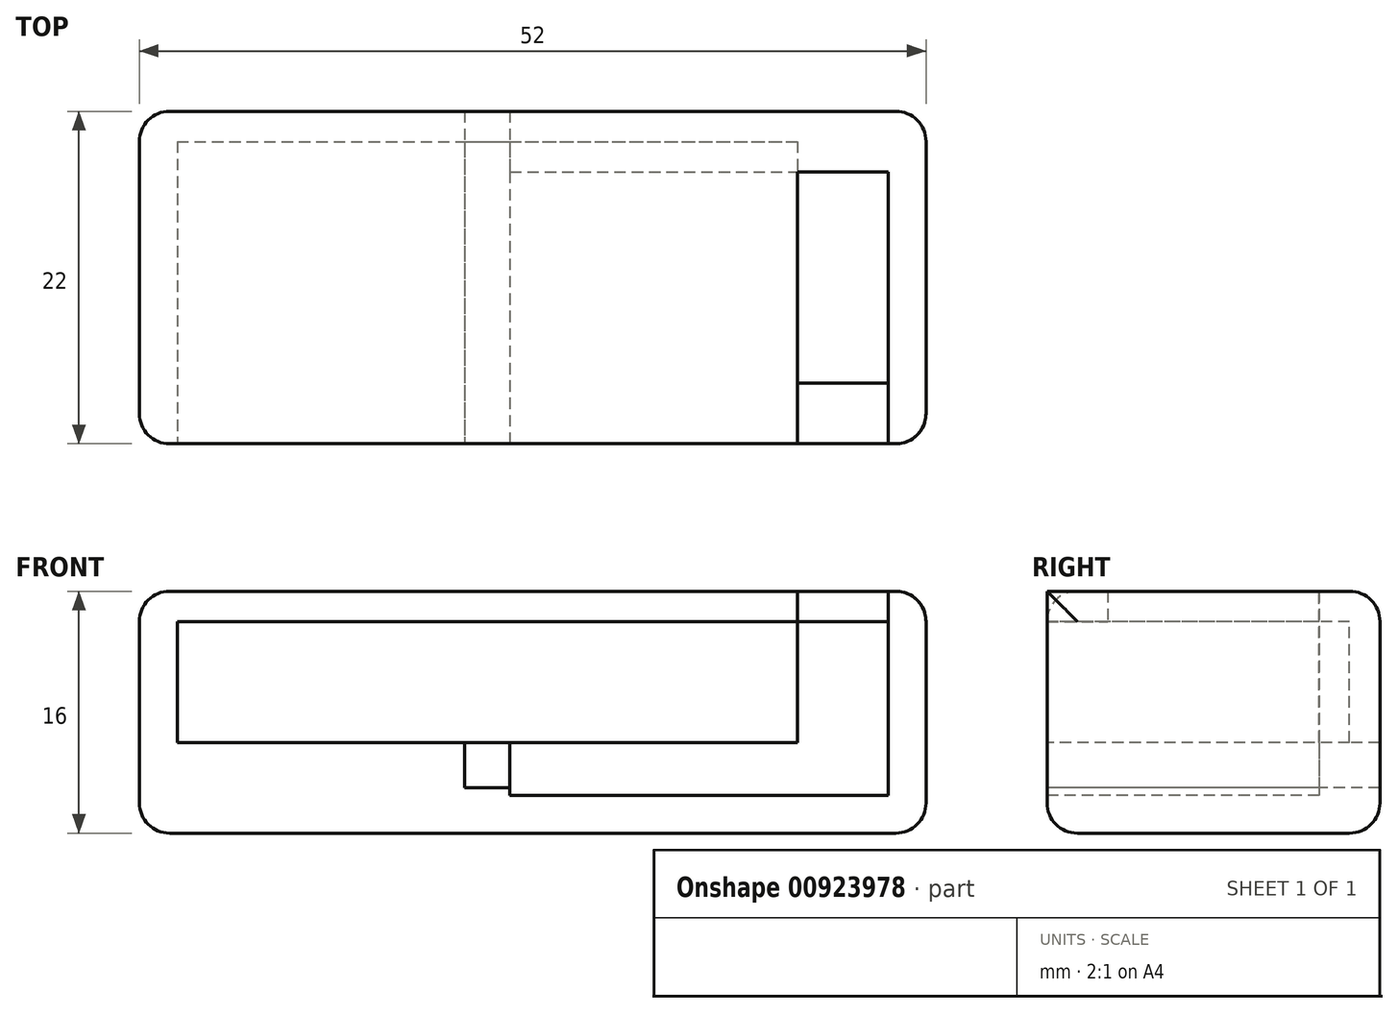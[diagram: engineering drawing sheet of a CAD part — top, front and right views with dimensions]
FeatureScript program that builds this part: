
annotation { "Feature Type Name" : "Feature", "Feature Type Description" : "" }
export const myFeature = defineFeature(function(context is Context, id is Id, definition is map)
    precondition{}
    {
        {
            var Q0;
            Q0=qCreatedBy(makeId("Top.planeOp"),FACE);
            var sketch = newSketch(context, id + "F0", { "sketchPlane" : qUnion([Q0])});
            skLineSegment(sketch, "E0.bottom", {"start": v(26, -11) * mm, "end": v(-26, -11) * mm});
            skLineSegment(sketch, "E0.top", {"start": v(26, 11) * mm, "end": v(-26, 11) * mm});
            skLineSegment(sketch, "E0.left", {"start": v(26, -11) * mm, "end": v(26, 11) * mm});
            skLineSegment(sketch, "E0.right", {"start": v(-26, -11) * mm, "end": v(-26, 11) * mm});
            skPoint(sketch, "E0.middle", {"position": v(0, 0) * mm});
            skSolve(sketch);
        }
        {
            var Q0;
            Q0 = qSketchRegion(id + "F0", true);
            extrude(context, id + "F1", {"entities" : qUnion([Q0]), "depth" : 16 * mm, "offsetDistance" : 25 * mm});
        }
        {
            var Q0;
            Q0=makeQuery(id+"F1.opExtrude","SWEPT_FACE",FACE,{"disambiguationData":[OSD([sQuery(id+"F0.wireOp",EDGE,"E0.bottom")])]});
            var sketch = newSketch(context, id + "F2", { "sketchPlane" : qUnion([Q0])});
            skLineSegment(sketch, "E1.bottom", {"start": v(-23.5, 6) * mm, "end": v(17.5, 6) * mm});
            skLineSegment(sketch, "E1.top", {"start": v(-23.5, 14) * mm, "end": v(17.5, 14) * mm});
            skLineSegment(sketch, "E1.left", {"start": v(-23.5, 6) * mm, "end": v(-23.5, 14) * mm});
            skLineSegment(sketch, "E1.right", {"start": v(17.5, 6) * mm, "end": v(17.5, 14) * mm});
            skSolve(sketch);
        }
        {
            var Q0;
            Q0 = qSketchRegion(id + "F2", true);
            extrude(context, id + "F3", {"entities" : qUnion([Q0]), "operationType" : NewBodyOperationType.REMOVE, "oppositeDirection" : true, "depth" : 20 * mm, "offsetDistance" : 25 * mm});
        }
        {
            var Q0;
            Q0=makeQuery(id+"F1.opExtrude","SWEPT_FACE",FACE,{"disambiguationData":[OSD([sQuery(id+"F0.wireOp",EDGE,"E0.bottom")])]});
            var sketch = newSketch(context, id + "F4", { "sketchPlane" : qUnion([Q0])});
            skLineSegment(sketch, "E2.bottom", {"start": v(-1.5, 6) * mm, "end": v(23.5, 6) * mm});
            skLineSegment(sketch, "E2.top", {"start": v(-1.5, 2.5) * mm, "end": v(23.5, 2.5) * mm});
            skLineSegment(sketch, "E2.left", {"start": v(-1.5, 6) * mm, "end": v(-1.5, 2.5) * mm});
            skLineSegment(sketch, "E2.right", {"start": v(23.5, 6) * mm, "end": v(23.5, 2.5) * mm});
            skLineSegment(sketch, "E3.bottom", {"start": v(17.5, 6) * mm, "end": v(23.5, 6) * mm});
            skLineSegment(sketch, "E3.top", {"start": v(17.5, 16) * mm, "end": v(23.5, 16) * mm});
            skLineSegment(sketch, "E3.left", {"start": v(17.5, 6) * mm, "end": v(17.5, 16) * mm});
            skLineSegment(sketch, "E3.right", {"start": v(23.5, 6) * mm, "end": v(23.5, 16) * mm});
            skSolve(sketch);
        }
        {
            var Q0;
            Q0 = qSketchRegion(id + "F4", true);
            extrude(context, id + "F5", {"entities" : qUnion([Q0]), "operationType" : NewBodyOperationType.REMOVE, "oppositeDirection" : true, "depth" : 18 * mm, "offsetDistance" : 25 * mm});
        }
        {
            var Q0;
            Q0=makeQuery(id+"F1.opExtrude","SWEPT_FACE",FACE,{"disambiguationData":[OSD([sQuery(id+"F0.wireOp",EDGE,"E0.bottom")])]});
            var sketch = newSketch(context, id + "F6", { "sketchPlane" : qUnion([Q0])});
            skLineSegment(sketch, "E4.bottom", {"start": v(-1.5, 6) * mm, "end": v(-4.5, 6) * mm});
            skLineSegment(sketch, "E4.top", {"start": v(-1.5, 3) * mm, "end": v(-4.5, 3) * mm});
            skLineSegment(sketch, "E4.left", {"start": v(-1.5, 6) * mm, "end": v(-1.5, 3) * mm});
            skLineSegment(sketch, "E4.right", {"start": v(-4.5, 6) * mm, "end": v(-4.5, 3) * mm});
            skSolve(sketch);
        }
        {
            var Q0;
            Q0 = qSketchRegion(id + "F6", true);
            extrude(context, id + "F7", {"entities" : qUnion([Q0]), "operationType" : NewBodyOperationType.REMOVE, "endBound" : BoundingType.UP_TO_NEXT, "oppositeDirection" : true, "depth" : 25 * mm, "offsetDistance" : 25 * mm});
        }
        {
            var Q0;
            Q0=makeQuery(id+"F5.boolean.opBoolean","COPY",FACE,{"derivedFrom":makeQuery(id+"F5.opExtrude","SWEPT_FACE",FACE,{"disambiguationData":[OSD([sQuery(id+"F4.wireOp",EDGE,"E2.right"),sQuery(id+"F4.wireOp",EDGE,"E3.right")])]})});
            var sketch = newSketch(context, id + "F8", { "sketchPlane" : qUnion([Q0])});
            skLineSegment(sketch, "E5.bottom", {"start": v(11, 16) * mm, "end": v(7, 16) * mm});
            skLineSegment(sketch, "E5.top", {"start": v(11, 14) * mm, "end": v(7, 14) * mm});
            skLineSegment(sketch, "E5.left", {"start": v(11, 16) * mm, "end": v(11, 14) * mm});
            skLineSegment(sketch, "E5.right", {"start": v(7, 16) * mm, "end": v(7, 14) * mm});
            skSolve(sketch);
        }
        {
            var Q0;
            Q0 = qSketchRegion(id + "F8", true);
            extrude(context, id + "F9", {"entities" : qUnion([Q0]), "depth" : 6 * mm, "offsetDistance" : 25 * mm});
        }
        {
            var Q0;
            Q0=makeQuery(id+"F1.opExtrude","CAP_EDGE",EDGE,{"disambiguationData":[OSD([sQuery(id+"F0.wireOp",EDGE,"E0.right")])],"isStart":true});
            var Q1;
            Q1=makeQuery(id+"F1.opExtrude","SWEPT_EDGE",EDGE,{"disambiguationData":[OSD([sQuery(id+"F0.wireOp",EDGE,"E0.bottom"),sQuery(id+"F0.wireOp",EDGE,"E0.right")])]});
            var Q2;
            {var subQ0=sQuery(id+"F0.wireOp",EDGE,"E0.bottom");var subQ1=sQuery(id+"F0.wireOp",EDGE,"E0.right");Q2=makeQuery(id+"F5.boolean.opBoolean","SPLIT",EDGE,{"disambiguationData":[TD([makeQuery(id+"F1.opExtrude","SWEPT_FACE",FACE,{"disambiguationData":[OSD([subQ1])]})])],"derivedFrom":makeQuery(id+"F1.opExtrude","CAP_EDGE",EDGE,{"disambiguationData":[OSD([subQ0])],"isStart":false})});}
            var Q3;
            Q3=makeQuery(id+"F1.opExtrude","CAP_EDGE",EDGE,{"disambiguationData":[OSD([sQuery(id+"F0.wireOp",EDGE,"E0.right")])],"isStart":false});
            var Q4;
            Q4=makeQuery(id+"F1.opExtrude","CAP_EDGE",EDGE,{"disambiguationData":[OSD([sQuery(id+"F0.wireOp",EDGE,"E0.bottom")])],"isStart":true});
            var Q5;
            Q5=makeQuery(id+"F1.opExtrude","SWEPT_EDGE",EDGE,{"disambiguationData":[OSD([sQuery(id+"F0.wireOp",EDGE,"E0.bottom"),sQuery(id+"F0.wireOp",EDGE,"E0.left")])]});
            var Q6;
            Q6=makeQuery(id+"F1.opExtrude","CAP_EDGE",EDGE,{"disambiguationData":[OSD([sQuery(id+"F0.wireOp",EDGE,"E0.left")])],"isStart":false});
            var Q7;
            Q7=makeQuery(id+"F1.opExtrude","SWEPT_EDGE",EDGE,{"disambiguationData":[OSD([sQuery(id+"F0.wireOp",EDGE,"E0.top"),sQuery(id+"F0.wireOp",EDGE,"E0.left")])]});
            var Q8;
            Q8=makeQuery(id+"F1.opExtrude","CAP_EDGE",EDGE,{"disambiguationData":[OSD([sQuery(id+"F0.wireOp",EDGE,"E0.left")])],"isStart":true});
            var Q9;
            Q9=makeQuery(id+"F1.opExtrude","CAP_EDGE",EDGE,{"disambiguationData":[OSD([sQuery(id+"F0.wireOp",EDGE,"E0.top")])],"isStart":false});
            var Q10;
            Q10=makeQuery(id+"F1.opExtrude","SWEPT_EDGE",EDGE,{"disambiguationData":[OSD([sQuery(id+"F0.wireOp",EDGE,"E0.top"),sQuery(id+"F0.wireOp",EDGE,"E0.right")])]});
            var Q11;
            Q11=makeQuery(id+"F1.opExtrude","CAP_EDGE",EDGE,{"disambiguationData":[OSD([sQuery(id+"F0.wireOp",EDGE,"E0.top")])],"isStart":true});
            var Q12;
            Q12=makeQuery(id+"F7.boolean.opBoolean","COPY",EDGE,{"derivedFrom":makeQuery(id+"F7.opExtrude","CAP_EDGE",EDGE,{"disambiguationData":[OSD([sQuery(id+"F6.wireOp",EDGE,"E4.bottom")])],"isStart":false})});
            var Q13;
            Q13=makeQuery(id+"F7.boolean.opBoolean","COPY",EDGE,{"derivedFrom":makeQuery(id+"F7.opExtrude","CAP_EDGE",EDGE,{"disambiguationData":[OSD([sQuery(id+"F6.wireOp",EDGE,"E4.right")])],"isStart":false})});
            var Q14;
            Q14=makeQuery(id+"F7.boolean.opBoolean","COPY",EDGE,{"derivedFrom":makeQuery(id+"F7.opExtrude","CAP_EDGE",EDGE,{"disambiguationData":[OSD([sQuery(id+"F6.wireOp",EDGE,"E4.left")])],"isStart":false})});
            var Q15;
            Q15=makeQuery(id+"F7.boolean.opBoolean","COPY",EDGE,{"derivedFrom":makeQuery(id+"F7.opExtrude","CAP_EDGE",EDGE,{"disambiguationData":[OSD([sQuery(id+"F6.wireOp",EDGE,"E4.top")])],"isStart":false})});
            fillet(context, id + "F10", {"entities" : qUnion([Q0, Q1, Q2, Q3, Q4, Q5, Q6, Q7, Q8, Q9, Q10, Q11, Q12, Q13, Q14, Q15]), "radius" : 2 * mm, "tangentPropagation" : true, "allowEdgeOverflow" : false});
        }
    });
